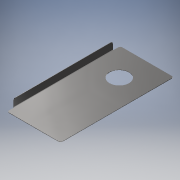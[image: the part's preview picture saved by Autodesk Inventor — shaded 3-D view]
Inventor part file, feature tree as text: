
AUTODESK INVENTOR PART (.ipt)
format: ipt  version: 2018 (Build 220112000, 112)  size: 153,088 bytes
history: native  units: mm
features: other x11, sketch x4, hole x1
ambient origin geometry x8: Origin, YZ Plane, XZ Plane, XY Plane, X Axis, Y Axis, Z Axis, Center Point
bodies: Solido1 (feature_tree)
feature tree (16):
  other  "Faccia1"
  other  "Flangia1"
  other  "Flangia2"
  other  "Arrotondamento angolo1"
  hole  "Foro1"  [1 undecoded]
  sketch  "Schizzo1"
  other  "Piano1"
  sketch  "Schizzo2"
  other  "Piano2"
  other  "Piega (Bend)1"
  other  "Angolo1"
  sketch  "Schizzo3"
  other  "Piano3"
  other  "Piega (Bend)2"
  other  "Angolo2"
  sketch  "Schizzo4"
note: 1 required parameter value undecoded (feature->parameter linkage not recoverable at this tier; creation-order binding heuristic only, values carry confidence <= 0.55)
